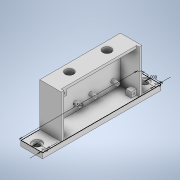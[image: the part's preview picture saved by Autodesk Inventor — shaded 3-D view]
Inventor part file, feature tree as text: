
AUTODESK INVENTOR PART (.ipt)
format: ipt  version: 2020 (Build 240168000, 168)  size: 315,904 bytes
history: native  units: in
note: dims shown in document units (in); Inventor stores cm internally (conversion verified against a paired STEP export)
features: sketch x11, extrude x7, hole x5, projected_geometry x2
ambient origin geometry x8: Origin, YZ Plane, XZ Plane, XY Plane, X Axis, Y Axis, Z Axis, Center Point
bodies: Solid1 (feature_tree)
feature tree (25):
  sketch  "Sketch1"  dims[d0=1.0in d1=5.5in]
  extrude  "Extrusion1"  Depth=5.5in
  hole  "Hole1"  [1 undecoded]
  extrude  "Extrusion2"  Depth=1.0in
  extrude  "Extrusion3"  Depth=3.5in
  extrude  "Extrusion4"  Depth=0.125in
  hole  "Hole2"  [1 undecoded]
  hole  "Hole3"  [1 undecoded]
  extrude  "Extrusion6"  Depth=0.75in TaperAngle=0.0deg
  extrude  "Extrusion7"  Depth=0.875in
  extrude  "Extrusion8"  Depth=0.5in
  hole  "Hole4"  [1 undecoded]
  hole  "Hole5"  [1 undecoded]
  sketch  "Sketch2"  dims[d2=0.25in d3=0.25in]
  sketch  "Sketch3"  dims[d4=0.25in d5=0.0in]
  sketch  "Sketch4"  dims[d6=0.281in d7=0.75in d8=0.438in d9=0.0625in d10=0.5635in d11=0.25in d12=0.0in d13=1.0in]
  sketch  "Sketch5"  dims[d14=0.125in d15=3.5in]
  projected_geometry  "Projected Loop1"
  sketch  "Sketch6"  dims[d16=1.0in d17=0.125in]
  projected_geometry  "Projected Loop2"
  sketch  "Sketch8"  dims[d18=1.0in d19=0.125in]
  sketch  "Sketch9"  dims[d20=2.0in d21=0.0in d22=3.5in]
  sketch  "Sketch10"  dims[d23=0.125in d24=0.75in d25=0.0in]
  sketch  "Sketch11"  dims[d26=0.9375in d27=0.875in]
  sketch  "Sketch12"  dims[d28=1.75in d29=1.025in d30=1.125in d31=1.025in d32=1.125in d33=0.175in d34=0.175in d35=0.175in d36=0.175in d37=0.175in d38=0.175in d39=0.175in d40=0.25in d41=0.0in d42=0.07in d43=0.75in d44=0.438in d45=0.25in d46=0.5635in d47=0.375in d48=0.0in d49=1.225in d50=1.325in d51=1.225in d52=1.325in d53=0.425in d54=0.425in d55=0.4in d56=0.75in d57=0.438in d58=0.25in d59=0.5635in d60=0.375in d61=0.0in d66=0.125in d67=0.125in d68=0.125in d69=0.125in d70=0.325in d71=0.25in d72=0.0in d73=0.25in d74=0.25in d75=0.25in d76=0.25in d77=0.25in d78=0.25in d79=0.0in d80=0.25in d81=0.25in d82=0.25in d83=0.25in d84=0.25in d85=0.0in d86=0.125in d87=0.125in d88=0.125in d89=0.089in d90=0.75in d91=0.438in d92=0.25in d93=0.5635in d94=0.375in d95=0.0in d96=0.125in d97=0.125in d98=0.125in d99=0.125in d100=0.125in d101=0.125in d102=0.125in d103=0.089in d104=0.75in d105=0.438in d106=0.25in d107=0.5635in d108=0.25in d109=0.0in d62=0.5in d63=0.0344in d64=0.5in d65=0.0344in]
note: 5 required parameter values undecoded (feature->parameter linkage not recoverable at this tier; creation-order binding heuristic only, values carry confidence <= 0.55)
